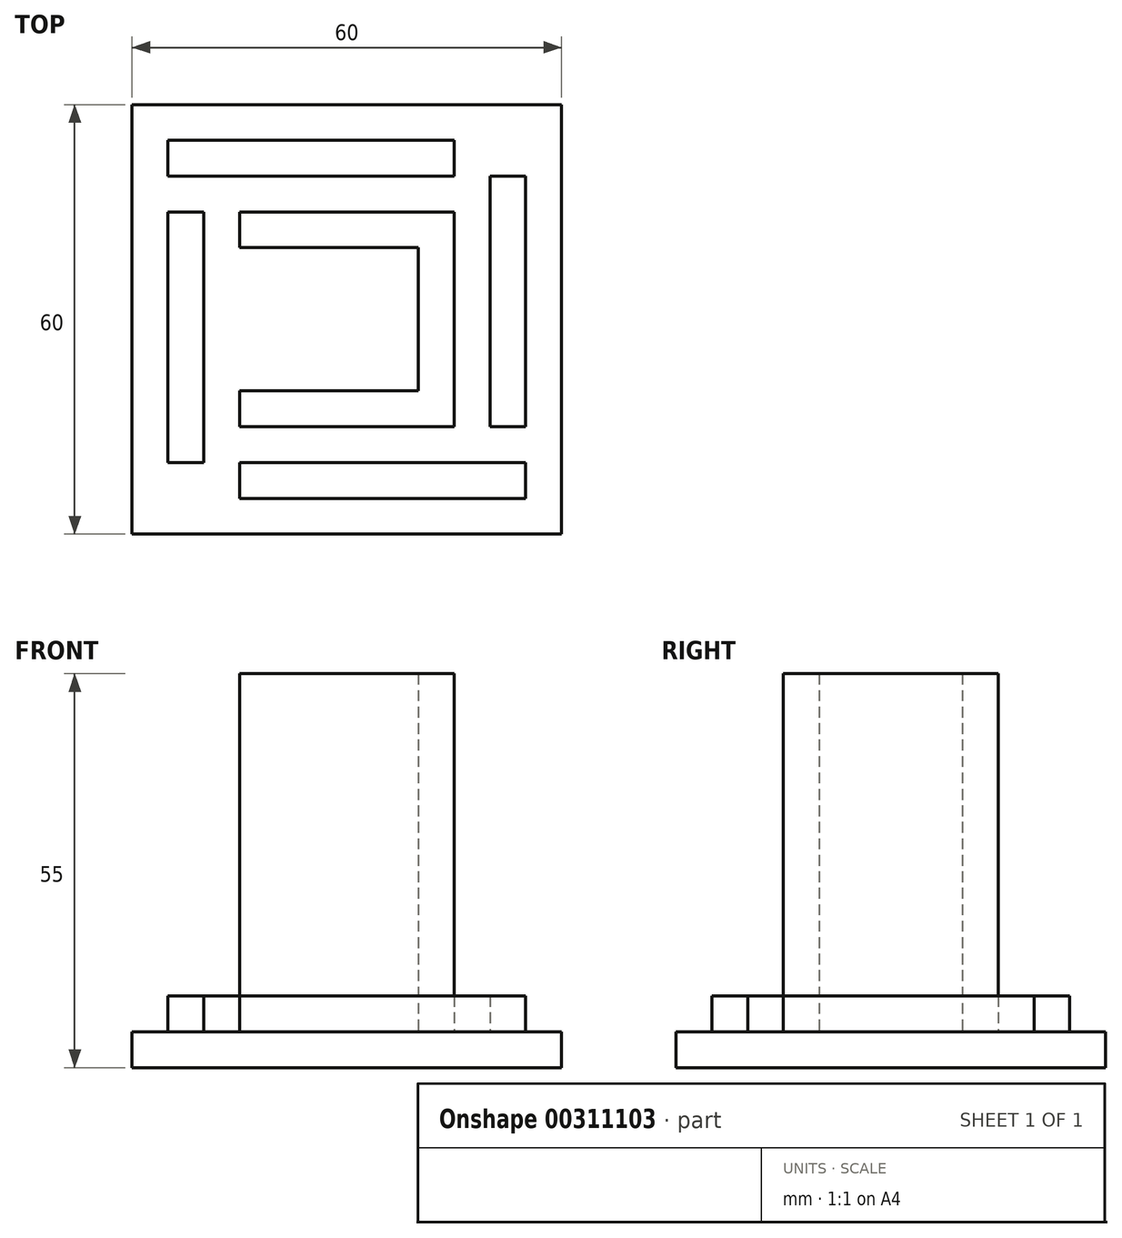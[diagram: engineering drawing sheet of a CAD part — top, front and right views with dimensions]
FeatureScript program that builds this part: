
annotation { "Feature Type Name" : "Feature", "Feature Type Description" : "" }
export const myFeature = defineFeature(function(context is Context, id is Id, definition is map)
    precondition{}
    {
        {
            var Q0;
            Q0=qCreatedBy(makeId("Top.planeOp"),FACE);
            var sketch = newSketch(context, id + "F0", { "sketchPlane" : qUnion([Q0])});
            skLineSegment(sketch, "E0.bottom", {"start": v(0, 0) * mm, "end": v(60, 0) * mm});
            skLineSegment(sketch, "E0.top", {"start": v(0, 60) * mm, "end": v(60, 60) * mm});
            skLineSegment(sketch, "E0.left", {"start": v(0, 0) * mm, "end": v(0, 60) * mm});
            skLineSegment(sketch, "E0.right", {"start": v(60, 0) * mm, "end": v(60, 60) * mm});
            skSolve(sketch);
        }
        {
            var Q0;
            Q0=makeQuery(id+"F0.imprint","IMPRINT",FACE,{"disambiguationData":[TD([[makeQuery(id+"F0.imprint","IMPRINT",EDGE,{"derivedFrom":sQuery(id+"F0.wireOp",EDGE,"E0.bottom")}),1.0]])]});
            extrude(context, id + "F1", {"entities" : qUnion([Q0]), "depth" : 5 * mm});
        }
        {
            var Q0;
            Q0=makeQuery(id+"F1.opExtrude","CAP_FACE",FACE,{"disambiguationData":[OSD([sQuery(id+"F0.wireOp",EDGE,"E0.bottom"),sQuery(id+"F0.wireOp",EDGE,"E0.top"),sQuery(id+"F0.wireOp",EDGE,"E0.left"),sQuery(id+"F0.wireOp",EDGE,"E0.right")])],"isStart":false});
            var sketch = newSketch(context, id + "F2", { "sketchPlane" : qUnion([Q0])});
            skLineSegment(sketch, "E1.bottom", {"start": v(15, 10) * mm, "end": v(55, 10) * mm});
            skLineSegment(sketch, "E1.top", {"start": v(15, 5) * mm, "end": v(55, 5) * mm});
            skLineSegment(sketch, "E1.left", {"start": v(15, 10) * mm, "end": v(15, 5) * mm});
            skLineSegment(sketch, "E1.right", {"start": v(55, 10) * mm, "end": v(55, 5) * mm});
            skLineSegment(sketch, "E2.bottom", {"start": v(55, 15) * mm, "end": v(50, 15) * mm});
            skLineSegment(sketch, "E2.top", {"start": v(55, 50) * mm, "end": v(50, 50) * mm});
            skLineSegment(sketch, "E2.left", {"start": v(55, 15) * mm, "end": v(55, 50) * mm});
            skLineSegment(sketch, "E2.right", {"start": v(50, 15) * mm, "end": v(50, 50) * mm});
            skLineSegment(sketch, "E3.bottom", {"start": v(45, 55) * mm, "end": v(5, 55) * mm});
            skLineSegment(sketch, "E3.top", {"start": v(45, 50) * mm, "end": v(5, 50) * mm});
            skLineSegment(sketch, "E3.left", {"start": v(45, 55) * mm, "end": v(45, 50) * mm});
            skLineSegment(sketch, "E3.right", {"start": v(5, 55) * mm, "end": v(5, 50) * mm});
            skLineSegment(sketch, "E4.bottom", {"start": v(5, 45) * mm, "end": v(10, 45) * mm});
            skLineSegment(sketch, "E4.top", {"start": v(5, 10) * mm, "end": v(10, 10) * mm});
            skLineSegment(sketch, "E4.left", {"start": v(5, 45) * mm, "end": v(5, 10) * mm});
            skLineSegment(sketch, "E4.right", {"start": v(10, 45) * mm, "end": v(10, 10) * mm});
            skSolve(sketch);
        }
        {
            var Q0;
            Q0=makeQuery(id+"F2.imprint","IMPRINT",FACE,{"disambiguationData":[TD([[makeQuery(id+"F2.imprint","IMPRINT",EDGE,{"derivedFrom":sQuery(id+"F2.wireOp",EDGE,"E1.bottom")}),-1.0]])]});
            var Q1;
            Q1=makeQuery(id+"F2.imprint","IMPRINT",FACE,{"disambiguationData":[TD([[makeQuery(id+"F2.imprint","IMPRINT",EDGE,{"derivedFrom":sQuery(id+"F2.wireOp",EDGE,"E2.bottom")}),-1.0]])]});
            var Q2;
            Q2=makeQuery(id+"F2.imprint","IMPRINT",FACE,{"disambiguationData":[TD([[makeQuery(id+"F2.imprint","IMPRINT",EDGE,{"derivedFrom":sQuery(id+"F2.wireOp",EDGE,"E3.bottom")}),1.0]])]});
            var Q3;
            Q3=makeQuery(id+"F2.imprint","IMPRINT",FACE,{"disambiguationData":[TD([[makeQuery(id+"F2.imprint","IMPRINT",EDGE,{"derivedFrom":sQuery(id+"F2.wireOp",EDGE,"E4.bottom")}),-1.0]])]});
            extrude(context, id + "F3", {"entities" : qUnion([Q0, Q1, Q2, Q3]), "operationType" : NewBodyOperationType.ADD, "depth" : 5 * mm});
        }
        {
            var Q0;
            Q0=makeQuery(id+"F1.opExtrude","CAP_FACE",FACE,{"disambiguationData":[OSD([sQuery(id+"F0.wireOp",EDGE,"E0.bottom"),sQuery(id+"F0.wireOp",EDGE,"E0.top"),sQuery(id+"F0.wireOp",EDGE,"E0.left"),sQuery(id+"F0.wireOp",EDGE,"E0.right")])],"isStart":false});
            var sketch = newSketch(context, id + "F4", { "sketchPlane" : qUnion([Q0])});
            skLineSegment(sketch, "E5.bottom", {"start": v(40, 45) * mm, "end": v(15, 45) * mm});
            skLineSegment(sketch, "E5.top", {"start": v(40, 40) * mm, "end": v(15, 40) * mm});
            skLineSegment(sketch, "E5.left", {"start": v(40, 45) * mm, "end": v(40, 40) * mm});
            skLineSegment(sketch, "E5.right", {"start": v(15, 45) * mm, "end": v(15, 40) * mm});
            skLineSegment(sketch, "E6.bottom", {"start": v(40, 45) * mm, "end": v(45, 45) * mm});
            skLineSegment(sketch, "E6.top", {"start": v(40, 15) * mm, "end": v(45, 15) * mm});
            skLineSegment(sketch, "E6.left", {"start": v(40, 45) * mm, "end": v(40, 15) * mm});
            skLineSegment(sketch, "E6.right", {"start": v(45, 45) * mm, "end": v(45, 15) * mm});
            skLineSegment(sketch, "E7.bottom", {"start": v(40, 15) * mm, "end": v(15, 15) * mm});
            skLineSegment(sketch, "E7.top", {"start": v(40, 20) * mm, "end": v(15, 20) * mm});
            skLineSegment(sketch, "E7.left", {"start": v(40, 15) * mm, "end": v(40, 20) * mm});
            skLineSegment(sketch, "E7.right", {"start": v(15, 15) * mm, "end": v(15, 20) * mm});
            skSolve(sketch);
        }
        {
            var Q0;
            {var subQ3=sQuery(id+"F4.wireOp",EDGE,"E6.bottom");Q0=makeQuery(id+"F4.imprint","IMPRINT",FACE,{"disambiguationData":[TD([[makeQuery(id+"F4.imprint","IMPRINT",EDGE,{"derivedFrom":subQ3}),-1.0]])]});}
            var Q1;
            {var subQ0=sQuery(id+"F4.wireOp",EDGE,"E5.bottom");Q1=makeQuery(id+"F4.imprint","IMPRINT",FACE,{"disambiguationData":[TD([[makeQuery(id+"F4.imprint","IMPRINT",EDGE,{"derivedFrom":subQ0}),1.0]])]});}
            var Q2;
            Q2=makeQuery(id+"F4.imprint","IMPRINT",FACE,{"disambiguationData":[TD([[makeQuery(id+"F4.imprint","IMPRINT",EDGE,{"derivedFrom":sQuery(id+"F4.wireOp",EDGE,"E7.bottom")}),-1.0]])]});
            extrude(context, id + "F5", {"entities" : qUnion([Q0, Q1, Q2]), "operationType" : NewBodyOperationType.ADD, "depth" : 50 * mm});
        }
    });
